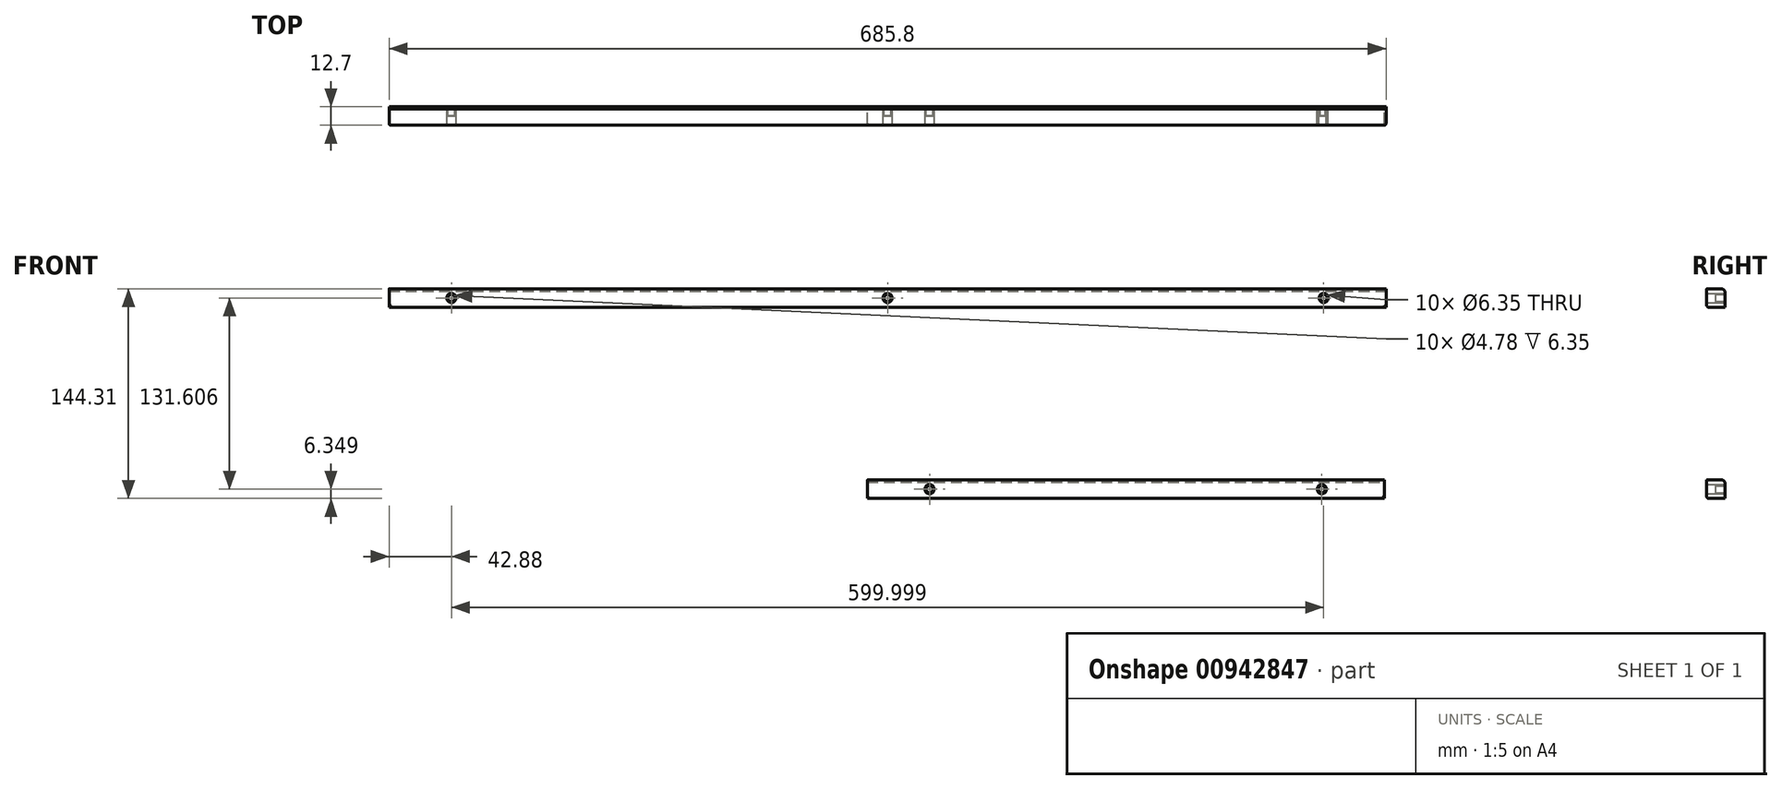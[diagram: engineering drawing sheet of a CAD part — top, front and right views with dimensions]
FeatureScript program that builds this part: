
annotation { "Feature Type Name" : "Feature", "Feature Type Description" : "" }
export const myFeature = defineFeature(function(context is Context, id is Id, definition is map)
    precondition{}
    {
        {
            var Q0;
            Q0=qCreatedBy(makeId("Front.planeOp"),FACE);
            var sketch = newSketch(context, id + "F0", { "sketchPlane" : qUnion([Q0])});
            skLineSegment(sketch, "E0.bottom", {"start": v(-634.49, 30.27) * mm, "end": v(51.31, 30.27) * mm});
            skLineSegment(sketch, "E0.top", {"start": v(-634.49, 17.57) * mm, "end": v(51.31, 17.57) * mm});
            skLineSegment(sketch, "E0.left", {"start": v(-634.49, 30.27) * mm, "end": v(-634.49, 17.57) * mm});
            skLineSegment(sketch, "E0.right", {"start": v(51.31, 30.27) * mm, "end": v(51.31, 17.57) * mm});
            skLineSegment(sketch, "E1.bottom", {"start": v(-305.56, -101.34) * mm, "end": v(50.04, -101.34) * mm});
            skLineSegment(sketch, "E1.top", {"start": v(-305.56, -114.04) * mm, "end": v(50.04, -114.04) * mm});
            skLineSegment(sketch, "E1.left", {"start": v(-305.56, -101.34) * mm, "end": v(-305.56, -114.04) * mm});
            skLineSegment(sketch, "E1.right", {"start": v(50.04, -101.34) * mm, "end": v(50.04, -114.04) * mm});
            skCircle(sketch, "E2", {"center": v(8.39, 23.92) * mm, "radius": 3.17 * mm});
            skCircle(sketch, "E3", {"center": v(8.39, 23.92) * mm, "radius": 2.39 * mm});
            skCircle(sketch, "E4", {"center": v(-591.61, 23.92) * mm, "radius": 3.17 * mm});
            skCircle(sketch, "E5", {"center": v(-591.61, 23.92) * mm, "radius": 2.39 * mm});
            skCircle(sketch, "E6", {"center": v(-291.59, 23.92) * mm, "radius": 3.17 * mm});
            skCircle(sketch, "E7", {"center": v(-291.59, 23.92) * mm, "radius": 2.39 * mm});
            skCircle(sketch, "E8", {"center": v(7.12, -107.7) * mm, "radius": 3.17 * mm});
            skCircle(sketch, "E9", {"center": v(7.12, -107.7) * mm, "radius": 2.39 * mm});
            skCircle(sketch, "E10", {"center": v(-262.68, -107.7) * mm, "radius": 3.17 * mm});
            skCircle(sketch, "E11", {"center": v(-262.68, -107.7) * mm, "radius": 2.39 * mm});
            skSolve(sketch);
        }
        {
            var Q0;
            Q0=makeQuery(id+"F0.imprint","IMPRINT",FACE,{"disambiguationData":[TD([[makeQuery(id+"F0.imprint","IMPRINT",EDGE,{"derivedFrom":sQuery(id+"F0.wireOp",EDGE,"E0.bottom")}),-1.0]])]});
            var Q1;
            Q1=makeQuery(id+"F0.imprint","IMPRINT",FACE,{"disambiguationData":[TD([[makeQuery(id+"F0.imprint","IMPRINT",EDGE,{"derivedFrom":sQuery(id+"F0.wireOp",EDGE,"E1.bottom")}),-1.0]])]});
            extrude(context, id + "F1", {"entities" : qUnion([Q0, Q1]), "depth" : 12.7 * mm, "offsetDistance" : 25.4 * mm});
        }
        {
            var Q0;
            Q0=makeQuery(id+"F0.imprint","IMPRINT",FACE,{"disambiguationData":[TD([[makeQuery(id+"F0.imprint","IMPRINT",EDGE,{"derivedFrom":sQuery(id+"F0.wireOp",EDGE,"E2")}),1.0]])]});
            var Q1;
            Q1=makeQuery(id+"F0.imprint","IMPRINT",FACE,{"disambiguationData":[TD([[makeQuery(id+"F0.imprint","IMPRINT",EDGE,{"derivedFrom":sQuery(id+"F0.wireOp",EDGE,"E6")}),1.0]])]});
            var Q2;
            Q2=makeQuery(id+"F0.imprint","IMPRINT",FACE,{"disambiguationData":[TD([[makeQuery(id+"F0.imprint","IMPRINT",EDGE,{"derivedFrom":sQuery(id+"F0.wireOp",EDGE,"E4")}),1.0]])]});
            var Q3;
            Q3=makeQuery(id+"F0.imprint","IMPRINT",FACE,{"disambiguationData":[TD([[makeQuery(id+"F0.imprint","IMPRINT",EDGE,{"derivedFrom":sQuery(id+"F0.wireOp",EDGE,"E10")}),1.0]])]});
            var Q4;
            Q4=makeQuery(id+"F0.imprint","IMPRINT",FACE,{"disambiguationData":[TD([[makeQuery(id+"F0.imprint","IMPRINT",EDGE,{"derivedFrom":sQuery(id+"F0.wireOp",EDGE,"E8")}),1.0]])]});
            extrude(context, id + "F2", {"entities" : qUnion([Q0, Q1, Q2, Q3, Q4]), "depth" : 6.35 * mm, "offsetDistance" : 25.4 * mm});
        }
        {
            var Q0;
            Q0=makeQuery(id+"F1.opExtrude","CAP_EDGE",EDGE,{"disambiguationData":[OSD([sQuery(id+"F0.wireOp",EDGE,"E1.top")])],"isStart":false});
            var Q1;
            Q1=makeQuery(id+"F1.opExtrude","CAP_EDGE",EDGE,{"disambiguationData":[OSD([sQuery(id+"F0.wireOp",EDGE,"E1.left")])],"isStart":false});
            var Q2;
            Q2=makeQuery(id+"F1.opExtrude","CAP_EDGE",EDGE,{"disambiguationData":[OSD([sQuery(id+"F0.wireOp",EDGE,"E1.right")])],"isStart":false});
            var Q3;
            Q3=makeQuery(id+"F1.opExtrude","CAP_EDGE",EDGE,{"disambiguationData":[OSD([sQuery(id+"F0.wireOp",EDGE,"E0.right")])],"isStart":false});
            var Q4;
            Q4=makeQuery(id+"F1.opExtrude","CAP_EDGE",EDGE,{"disambiguationData":[OSD([sQuery(id+"F0.wireOp",EDGE,"E0.left")])],"isStart":false});
            var Q5;
            Q5=makeQuery(id+"F1.opExtrude","CAP_EDGE",EDGE,{"disambiguationData":[OSD([sQuery(id+"F0.wireOp",EDGE,"E0.top")])],"isStart":false});
            fillet(context, id + "F3", {"entities" : qUnion([Q0, Q1, Q2, Q3, Q4, Q5]), "radius" : 1.27 * mm, "tangentPropagation" : true, "allowEdgeOverflow" : false});
        }
        {
            var Q0;
            Q0=makeQuery(id+"F1.opExtrude","CAP_EDGE",EDGE,{"disambiguationData":[OSD([sQuery(id+"F0.wireOp",EDGE,"E0.bottom")])],"isStart":true});
            var Q1;
            Q1=makeQuery(id+"F1.opExtrude","CAP_EDGE",EDGE,{"disambiguationData":[OSD([sQuery(id+"F0.wireOp",EDGE,"E1.bottom")])],"isStart":true});
            chamfer(context, id + "F4", {"entities" : qUnion([Q0, Q1]), "width" : 1.59 * mm, "tangentPropagation" : true});
        }
    });
